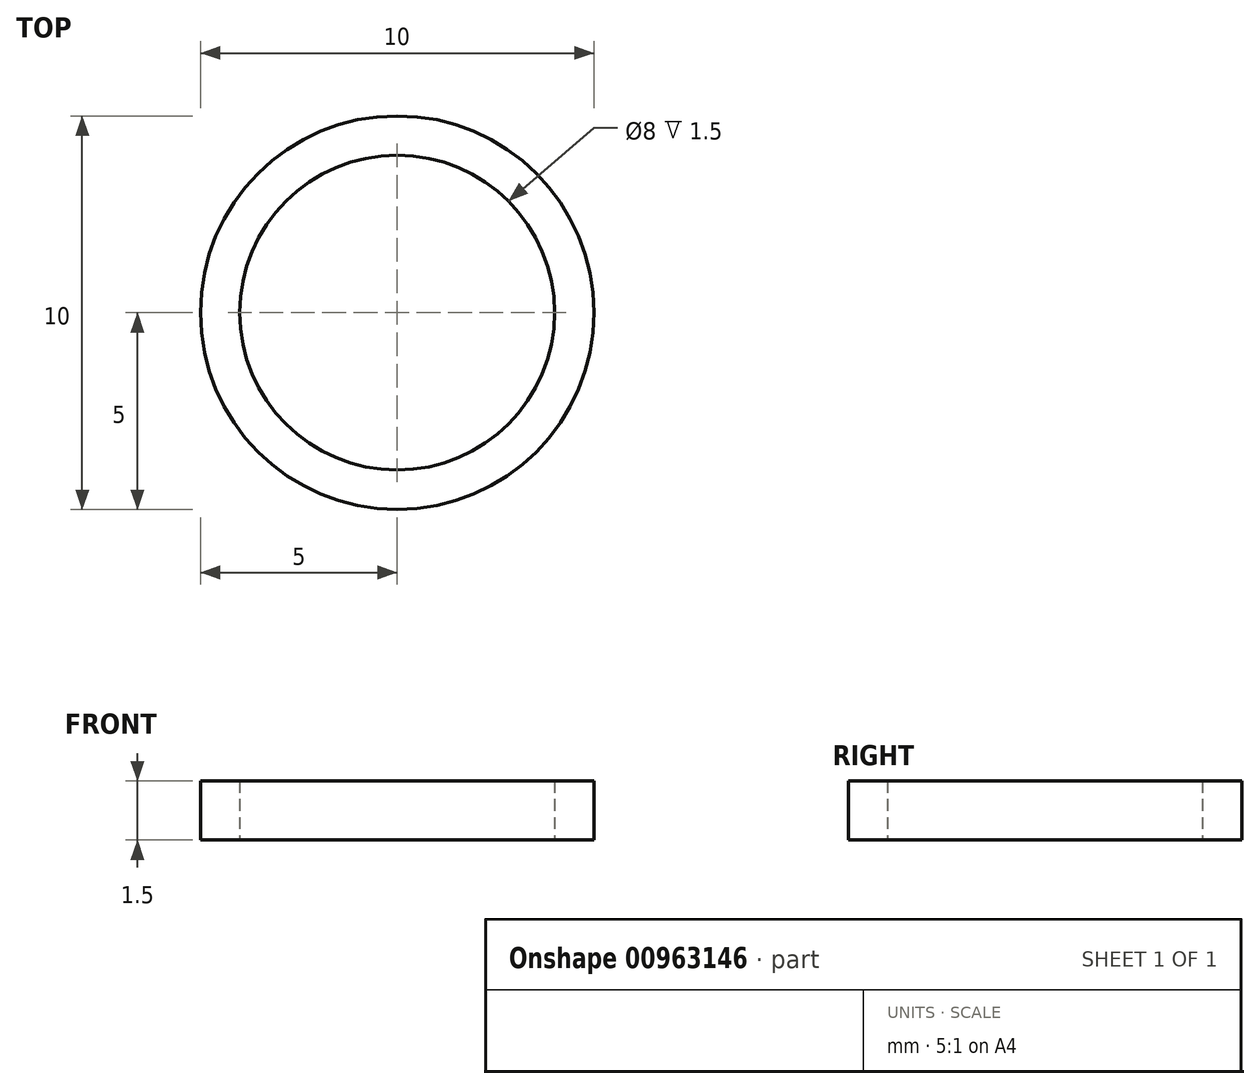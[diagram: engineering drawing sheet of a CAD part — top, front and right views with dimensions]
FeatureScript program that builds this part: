
annotation { "Feature Type Name" : "Feature", "Feature Type Description" : "" }
export const myFeature = defineFeature(function(context is Context, id is Id, definition is map)
    precondition{}
    {
        {
            var Q0;
            Q0=qCreatedBy(makeId("Top.planeOp"),FACE);
            cPlane(context, id + "F0", {"entities" : qUnion([Q0]), "cplaneType" : CPlaneType.OFFSET, "offset" : 25 * mm, "width" : 150 * mm, "height" : 150 * mm});
        }
        {
            var Q0;
            Q0=qCreatedBy(id+"F0.planeOp",FACE);
            var sketch = newSketch(context, id + "F1", { "sketchPlane" : qUnion([Q0])});
            skCircle(sketch, "E0", {"center": v(0, 0) * mm, "radius": 5 * mm});
            skCircle(sketch, "E1", {"center": v(0, 0) * mm, "radius": 4 * mm});
            skSolve(sketch);
        }
        {
            var Q0;
            Q0 = qSketchRegion(id + "F1", true);
            extrude(context, id + "F2", {"entities" : qUnion([Q0]), "depth" : 1.5 * mm, "offsetDistance" : 25 * mm});
        }
    });
